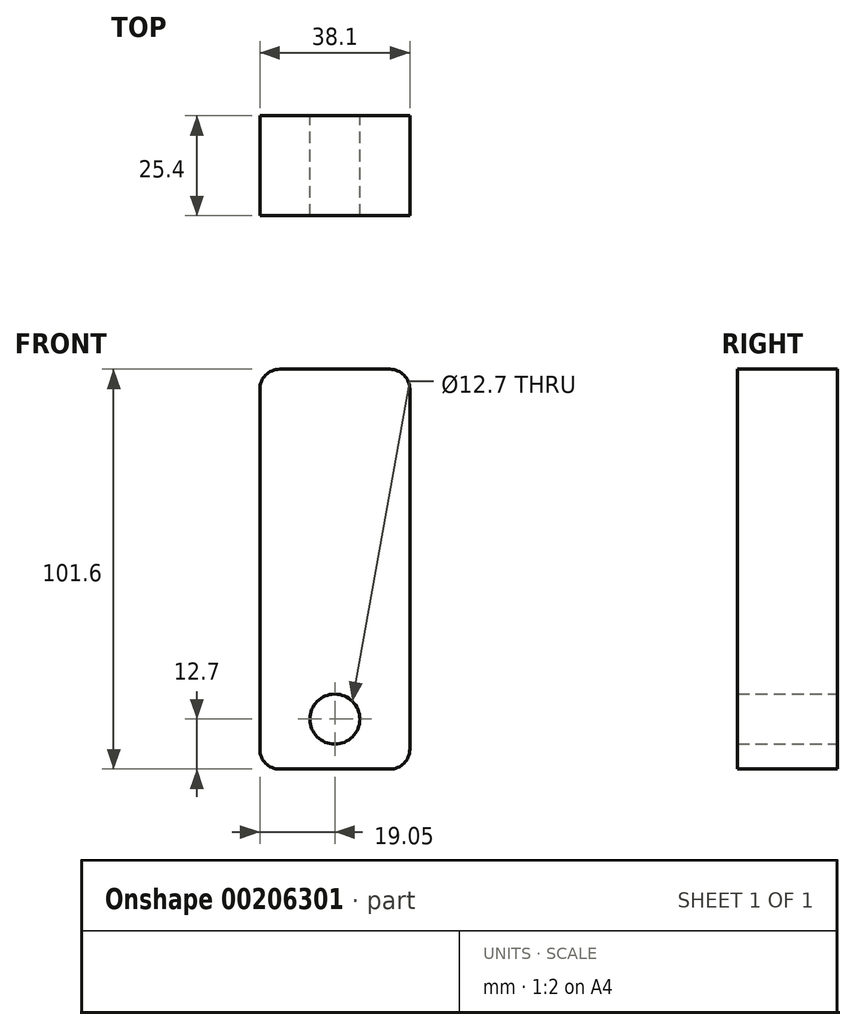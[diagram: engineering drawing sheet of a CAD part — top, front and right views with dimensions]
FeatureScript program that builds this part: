
annotation { "Feature Type Name" : "Feature", "Feature Type Description" : "" }
export const myFeature = defineFeature(function(context is Context, id is Id, definition is map)
    precondition{}
    {
        {
            var Q0;
            Q0=qCreatedBy(makeId("Front.planeOp"),FACE);
            var sketch = newSketch(context, id + "F0", { "sketchPlane" : qUnion([Q0])});
            skLineSegment(sketch, "E0.bottom", {"start": v(-19.05, 50.8) * mm, "end": v(19.05, 50.8) * mm});
            skLineSegment(sketch, "E0.top", {"start": v(-19.05, -50.8) * mm, "end": v(19.05, -50.8) * mm});
            skLineSegment(sketch, "E0.left", {"start": v(-19.05, 50.8) * mm, "end": v(-19.05, -50.8) * mm});
            skLineSegment(sketch, "E0.right", {"start": v(19.05, 50.8) * mm, "end": v(19.05, -50.8) * mm});
            skPoint(sketch, "E0.middle", {"position": v(0, 0) * mm});
            skCircle(sketch, "E1", {"center": v(0, -38.1) * mm, "radius": 6.35 * mm});
            skSolve(sketch);
        }
        {
            var Q0;
            Q0=makeQuery(id+"F0.imprint","IMPRINT",FACE,{"disambiguationData":[TD([[makeQuery(id+"F0.imprint","IMPRINT",EDGE,{"derivedFrom":sQuery(id+"F0.wireOp",EDGE,"E0.bottom")}),-1.0]])]});
            extrude(context, id + "F1", {"entities" : qUnion([Q0]), "endBound" : BoundingType.SYMMETRIC, "depth" : 25.4 * mm});
        }
        {
            var Q0;
            Q0=makeQuery(id+"F1.opExtrude","SWEPT_EDGE",EDGE,{"disambiguationData":[OSD([sQuery(id+"F0.wireOp",EDGE,"E0.bottom"),sQuery(id+"F0.wireOp",EDGE,"E0.left")])]});
            var Q1;
            Q1=makeQuery(id+"F1.opExtrude","SWEPT_EDGE",EDGE,{"disambiguationData":[OSD([sQuery(id+"F0.wireOp",EDGE,"E0.bottom"),sQuery(id+"F0.wireOp",EDGE,"E0.right")])]});
            var Q2;
            Q2=makeQuery(id+"F1.opExtrude","SWEPT_EDGE",EDGE,{"disambiguationData":[OSD([sQuery(id+"F0.wireOp",EDGE,"E0.top"),sQuery(id+"F0.wireOp",EDGE,"E0.right")])]});
            var Q3;
            Q3=makeQuery(id+"F1.opExtrude","SWEPT_EDGE",EDGE,{"disambiguationData":[OSD([sQuery(id+"F0.wireOp",EDGE,"E0.top"),sQuery(id+"F0.wireOp",EDGE,"E0.left")])]});
            fillet(context, id + "F2", {"entities" : qUnion([Q0, Q1, Q2, Q3]), "radius" : 5.08 * mm, "tangentPropagation" : true, "allowEdgeOverflow" : false});
        }
    });
